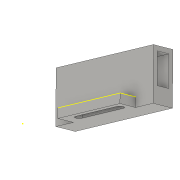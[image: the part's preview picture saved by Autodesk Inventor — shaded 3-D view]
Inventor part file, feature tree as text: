
AUTODESK INVENTOR PART (.ipt)
format: ipt  version: 2016 (Build 200138000, 138)  size: 140,288 bytes
history: native  units: mm
features: sketch x8, extrude x7
ambient origin geometry x8: Origin, YZ Plane, XZ Plane, XY Plane, X Axis, Y Axis, Z Axis, Center Point
bodies: Body1 (feature_tree)
feature tree (15):
  extrude  "Extrusion13"  Depth=28.0mm
  extrude  "Extrusion14"  Depth=13.0mm
  extrude  "Extrusion15"  Depth=13.0mm TaperAngle=0.0deg
  extrude  "Extrusion20"  Depth=17.0mm TaperAngle=0.0deg
  extrude  "Extrusion22"  Depth=8.0mm TaperAngle=0.0deg
  extrude  "Extrusion23"  Depth=12.0mm TaperAngle=0.0deg
  extrude  "Extrusion24"  [1 undecoded]
  sketch  "Skizze26"
  sketch  "Skizze14"  dims[d40=28.0mm d41=67.0mm]
  sketch  "Skizze15"  dims[d42=10.0mm d43=0.0mm d44=13.0mm]
  sketch  "Skizze16"  dims[d45=6.0mm d46=13.0mm d47=0.0mm]
  sketch  "Skizze21"  dims[d48=60.0mm d49=0.0mm d62=17.0mm d63=0.0mm]
  sketch  "Skizze23"  dims[d66=60.0mm d67=0.0mm d68=8.0mm d69=0.0mm]
  sketch  "Skizze24"  dims[d70=3.5mm d71=12.0mm d72=0.0mm]
  sketch  "Skizze25"
note: 1 required parameter value undecoded (feature->parameter linkage not recoverable at this tier; creation-order binding heuristic only, values carry confidence <= 0.55)
